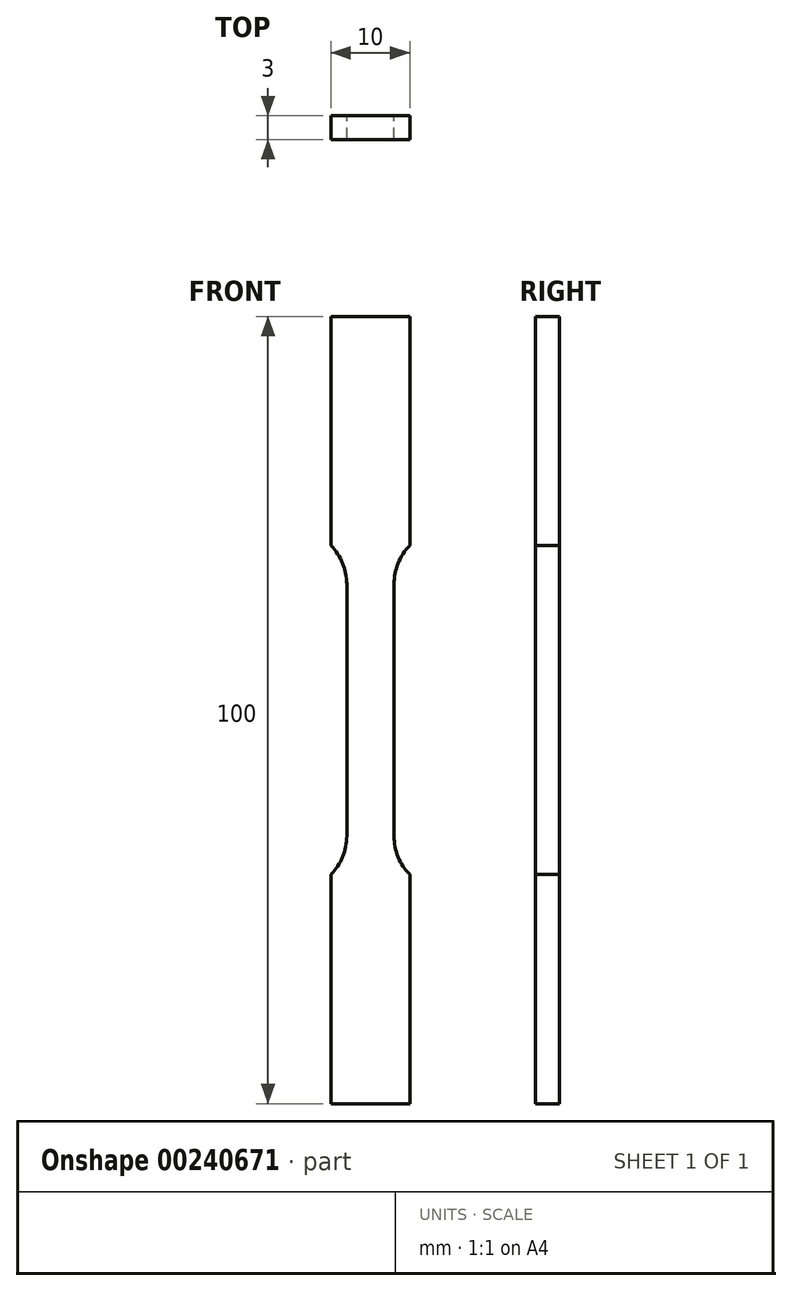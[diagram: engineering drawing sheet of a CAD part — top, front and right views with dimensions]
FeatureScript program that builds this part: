
annotation { "Feature Type Name" : "Feature", "Feature Type Description" : "" }
export const myFeature = defineFeature(function(context is Context, id is Id, definition is map)
    precondition{}
    {
        {
            var Q0;
            Q0=qCreatedBy(makeId("Front.planeOp"),FACE);
            var sketch = newSketch(context, id + "F0", { "sketchPlane" : qUnion([Q0])});
            skLineSegment(sketch, "E0.right", {"start": v(3, 0) * mm, "end": v(3, 16) * mm});
            skLineSegment(sketch, "E1.top", {"start": v(0, 50) * mm, "end": v(5, 50) * mm});
            skLineSegment(sketch, "E1.right", {"start": v(5, 20.9) * mm, "end": v(5, 50) * mm});
            skArc(sketch, "E2", {"start": v(3, 16) * mm, "mid": v(3.52, 18.65) * mm, "end": v(5, 20.9) * mm});
            skArc(sketch, "E3.MirrorCS", {"start": v(-3, 16) * mm, "mid": v(-3.52, 18.65) * mm, "end": v(-5, 20.9) * mm});
            skLineSegment(sketch, "E4.MirrorCS", {"start": v(0, 50) * mm, "end": v(-5, 50) * mm});
            skLineSegment(sketch, "E5.MirrorCS", {"start": v(-5, 20.9) * mm, "end": v(-5, 50) * mm});
            skLineSegment(sketch, "E6.MirrorCS", {"start": v(-3, 0) * mm, "end": v(-3, 16) * mm});
            skArc(sketch, "E7.MirrorCS", {"start": v(-3, -16) * mm, "mid": v(-3.52, -18.65) * mm, "end": v(-5, -20.9) * mm});
            skArc(sketch, "E8.MirrorCS", {"start": v(3, -16) * mm, "mid": v(3.52, -18.65) * mm, "end": v(5, -20.9) * mm});
            skLineSegment(sketch, "E9.MirrorCS", {"start": v(0, -50) * mm, "end": v(-5, -50) * mm});
            skLineSegment(sketch, "E10.MirrorCS", {"start": v(5, -20.9) * mm, "end": v(5, -50) * mm});
            skLineSegment(sketch, "E11.MirrorCS", {"start": v(0, -50) * mm, "end": v(5, -50) * mm});
            skLineSegment(sketch, "E12.MirrorCS", {"start": v(3, 0) * mm, "end": v(3, -16) * mm});
            skLineSegment(sketch, "E13.MirrorCS", {"start": v(-3, 0) * mm, "end": v(-3, -16) * mm});
            skLineSegment(sketch, "E14.MirrorCS", {"start": v(-5, -20.9) * mm, "end": v(-5, -50) * mm});
            skSolve(sketch);
        }
        {
            var Q0;
            Q0 = qSketchRegion(id + "F0", true);
            extrude(context, id + "F1", {"entities" : qUnion([Q0]), "depth" : 3 * mm});
        }
    });
